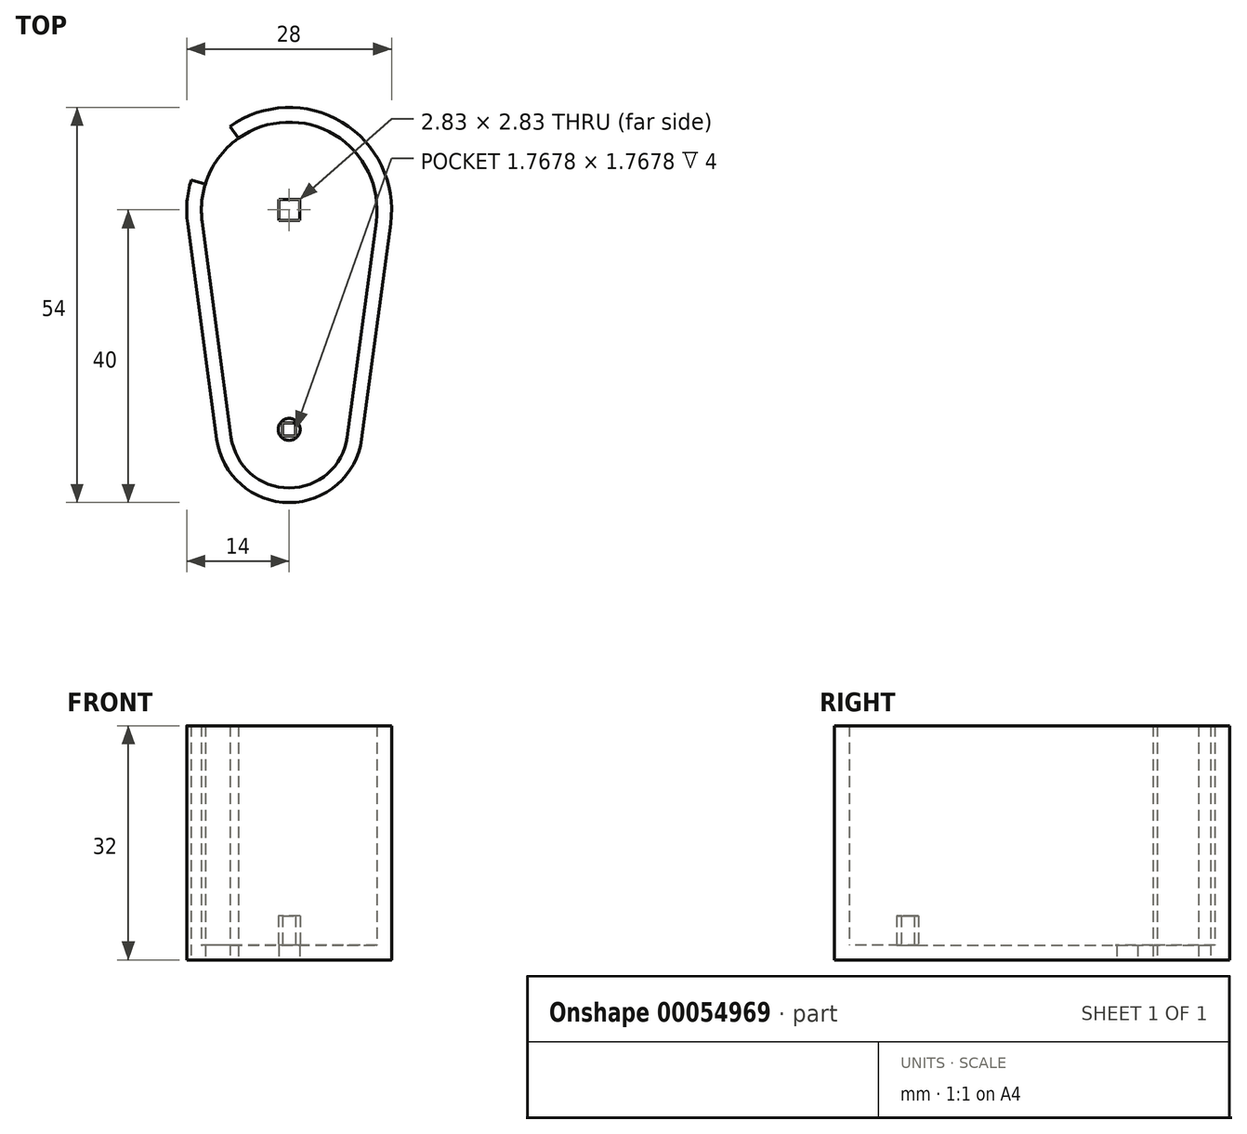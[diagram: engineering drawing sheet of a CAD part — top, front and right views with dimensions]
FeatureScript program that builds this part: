
annotation { "Feature Type Name" : "Feature", "Feature Type Description" : "" }
export const myFeature = defineFeature(function(context is Context, id is Id, definition is map)
    precondition{}
    {
        {
            var Q0;
            Q0=qCreatedBy(makeId("Top.planeOp"),FACE);
            var sketch = newSketch(context, id + "F0", { "sketchPlane" : qUnion([Q0])});
            skArc(sketch, "E0", {"start": v(13.87, -1.87) * mm, "mid": v(0, 14) * mm, "end": v(-13.87, -1.87) * mm});
            skArc(sketch, "E1", {"start": v(-9.91, -31.33) * mm, "mid": v(0, -40) * mm, "end": v(9.91, -31.33) * mm});
            skLineSegment(sketch, "E2", {"start": v(-13.87, -1.87) * mm, "end": v(-9.91, -31.33) * mm});
            skLineSegment(sketch, "E3", {"start": v(13.87, -1.87) * mm, "end": v(9.91, -31.33) * mm});
            skCircle(sketch, "E4", {"center": v(0, -30) * mm, "radius": 8 * mm});
            skCircle(sketch, "E5", {"center": v(0, 0) * mm, "radius": 12 * mm});
            skLineSegment(sketch, "E6", {"start": v(7.93, -31.07) * mm, "end": v(11.9, -1.6) * mm});
            skLineSegment(sketch, "E7", {"start": v(-7.93, -31.07) * mm, "end": v(-12.1, 0) * mm});
            skCircle(sketch, "E8", {"center": v(0, -30) * mm, "radius": 4.9 * mm});
            skCircle(sketch, "E9", {"center": v(0, -30) * mm, "radius": 2.95 * mm});
            skCircle(sketch, "E10", {"center": v(0, -30) * mm, "radius": 1.5 * mm});
            skCircle(sketch, "E11", {"center": v(0, 0) * mm, "radius": 4 * mm});
            skCircle(sketch, "E12", {"center": v(0, 0) * mm, "radius": 2.5 * mm});
            skLineSegment(sketch, "E13", {"start": v(-9.42, -20) * mm, "end": v(9.05, -20) * mm, "construction": true});
            skArc(sketch, "E14", {"start": v(-9.08, -22.48) * mm, "mid": v(-4.43, -19.6) * mm, "end": v(-9.68, -18.05) * mm});
            skArc(sketch, "E15", {"start": v(9.68, -18.05) * mm, "mid": v(4.43, -19.6) * mm, "end": v(9.08, -22.48) * mm});
            skArc(sketch, "E16", {"start": v(9.84, -16.83) * mm, "mid": v(3.44, -19.47) * mm, "end": v(8.92, -23.7) * mm});
            skArc(sketch, "E17", {"start": v(-8.92, -23.7) * mm, "mid": v(-3.44, -19.47) * mm, "end": v(-9.84, -16.83) * mm});
            skLineSegment(sketch, "E18", {"start": v(-8.1, 11.42) * mm, "end": v(-6.95, 9.78) * mm});
            skLineSegment(sketch, "E19", {"start": v(-13.39, 4.1) * mm, "end": v(-11.48, 3.5) * mm});
            skLineSegment(sketch, "E20.bottom", {"start": v(-1.41, 1.41) * mm, "end": v(1.41, 1.41) * mm});
            skLineSegment(sketch, "E20.top", {"start": v(-1.41, -1.41) * mm, "end": v(1.41, -1.41) * mm});
            skLineSegment(sketch, "E20.left", {"start": v(-1.41, 1.41) * mm, "end": v(-1.41, -1.41) * mm});
            skLineSegment(sketch, "E20.right", {"start": v(1.41, 1.41) * mm, "end": v(1.41, -1.41) * mm});
            skLineSegment(sketch, "E21.bottom", {"start": v(-0.88, -29.12) * mm, "end": v(0.88, -29.12) * mm});
            skLineSegment(sketch, "E21.top", {"start": v(-0.88, -30.88) * mm, "end": v(0.88, -30.88) * mm});
            skLineSegment(sketch, "E21.left", {"start": v(-0.88, -29.12) * mm, "end": v(-0.88, -30.88) * mm});
            skLineSegment(sketch, "E21.right", {"start": v(0.88, -29.12) * mm, "end": v(0.88, -30.88) * mm});
            skLineSegment(sketch, "E22", {"start": v(4, 0) * mm, "end": v(-4, 0) * mm, "construction": true});
            skLineSegment(sketch, "E23", {"start": v(0, 4) * mm, "end": v(0, -4) * mm, "construction": true});
            skLineSegment(sketch, "E24", {"start": v(-1.41, 1.41) * mm, "end": v(1.41, -1.41) * mm, "construction": true});
            skLineSegment(sketch, "E25", {"start": v(1.41, 1.41) * mm, "end": v(-1.41, -1.41) * mm, "construction": true});
            skLineSegment(sketch, "E26", {"start": v(-0.88, -30.88) * mm, "end": v(0.88, -29.12) * mm, "construction": true});
            skLineSegment(sketch, "E27", {"start": v(-0.88, -29.12) * mm, "end": v(0.88, -30.88) * mm, "construction": true});
            skLineSegment(sketch, "E28", {"start": v(0, -28.5) * mm, "end": v(0, -31.5) * mm, "construction": true});
            skLineSegment(sketch, "E29", {"start": v(-1.5, -30) * mm, "end": v(1.5, -30) * mm, "construction": true});
            skSolve(sketch);
        }
        {
            var Q0;
            Q0=makeQuery(id+"F0.imprint","IMPRINT",FACE,{"disambiguationData":[TD([[makeQuery(id+"F0.imprint","IMPRINT",EDGE,{"derivedFrom":sQuery(id+"F0.wireOp",EDGE,"E1")}),1.0]])]});
            extrude(context, id + "F1", {"entities" : qUnion([Q0]), "depth" : 32 * mm});
        }
        {
            var Q0;
            Q0=makeQuery(id+"F0.imprint","IMPRINT",FACE,{"disambiguationData":[TD([[makeQuery(id+"F0.imprint","IMPRINT",EDGE,{"derivedFrom":sQuery(id+"F0.wireOp",EDGE,"E11")}),-1.0]])]});
            var Q1;
            {var subQ3=sQuery(id+"F0.wireOp",EDGE,"E16");Q1=makeQuery(id+"F0.imprint","IMPRINT",FACE,{"disambiguationData":[TD([[makeQuery(id+"F0.imprint","IMPRINT",EDGE,{"derivedFrom":subQ3}),-1.0]])]});}
            var Q2;
            Q2=makeQuery(id+"F0.imprint","IMPRINT",FACE,{"disambiguationData":[TD([[makeQuery(id+"F0.imprint","IMPRINT",EDGE,{"derivedFrom":sQuery(id+"F0.wireOp",EDGE,"E8")}),-1.0]])]});
            var Q3;
            {var subQ0=sQuery(id+"F0.wireOp",EDGE,"E15");Q3=makeQuery(id+"F0.imprint","IMPRINT",FACE,{"disambiguationData":[TD([[makeQuery(id+"F0.imprint","IMPRINT",EDGE,{"derivedFrom":subQ0}),-1.0]])]});}
            var Q4;
            {var subQ0=sQuery(id+"F0.wireOp",EDGE,"E14");Q4=makeQuery(id+"F0.imprint","IMPRINT",FACE,{"disambiguationData":[TD([[makeQuery(id+"F0.imprint","IMPRINT",EDGE,{"derivedFrom":subQ0}),-1.0]])]});}
            var Q5;
            {var subQ0=sQuery(id+"F0.wireOp",EDGE,"E14");Q5=makeQuery(id+"F0.imprint","IMPRINT",FACE,{"disambiguationData":[TD([[makeQuery(id+"F0.imprint","IMPRINT",EDGE,{"derivedFrom":subQ0}),1.0]])]});}
            var Q6;
            Q6=makeQuery(id+"F0.imprint","IMPRINT",FACE,{"disambiguationData":[TD([[makeQuery(id+"F0.imprint","IMPRINT",EDGE,{"derivedFrom":sQuery(id+"F0.wireOp",EDGE,"E8")}),1.0]])]});
            var Q7;
            Q7=makeQuery(id+"F0.imprint","IMPRINT",FACE,{"disambiguationData":[TD([[makeQuery(id+"F0.imprint","IMPRINT",EDGE,{"derivedFrom":sQuery(id+"F0.wireOp",EDGE,"E9")}),1.0]])]});
            var Q8;
            Q8=makeQuery(id+"F0.imprint","IMPRINT",FACE,{"disambiguationData":[TD([[makeQuery(id+"F0.imprint","IMPRINT",EDGE,{"derivedFrom":sQuery(id+"F0.wireOp",EDGE,"E20.bottom")}),-1.0]])]});
            var Q9;
            Q9=makeQuery(id+"F0.imprint","IMPRINT",FACE,{"disambiguationData":[TD([[makeQuery(id+"F0.imprint","IMPRINT",EDGE,{"derivedFrom":sQuery(id+"F0.wireOp",EDGE,"E12")}),1.0]])]});
            var Q10;
            Q10=makeQuery(id+"F0.imprint","IMPRINT",FACE,{"disambiguationData":[TD([[makeQuery(id+"F0.imprint","IMPRINT",EDGE,{"derivedFrom":sQuery(id+"F0.wireOp",EDGE,"E11")}),1.0]])]});
            var Q11;
            Q11=makeQuery(id+"F0.imprint","IMPRINT",FACE,{"disambiguationData":[TD([[makeQuery(id+"F0.imprint","IMPRINT",EDGE,{"derivedFrom":sQuery(id+"F0.wireOp",EDGE,"E21.bottom")}),-1.0]])]});
            var Q12;
            Q12=makeQuery(id+"F0.imprint","IMPRINT",FACE,{"disambiguationData":[TD([[makeQuery(id+"F0.imprint","IMPRINT",EDGE,{"derivedFrom":sQuery(id+"F0.wireOp",EDGE,"E10")}),1.0]])]});
            var Q13;
            {var subQ0=sQuery(id+"F0.wireOp",EDGE,"E15");Q13=makeQuery(id+"F0.imprint","IMPRINT",FACE,{"disambiguationData":[TD([[makeQuery(id+"F0.imprint","IMPRINT",EDGE,{"derivedFrom":subQ0}),1.0]])]});}
            extrude(context, id + "F2", {"entities" : qUnion([Q0, Q1, Q2, Q3, Q4, Q5, Q6, Q7, Q8, Q9, Q10, Q11, Q12, Q13]), "operationType" : NewBodyOperationType.ADD, "depth" : 2 * mm});
        }
        {
            var Q0;
            Q0=makeQuery(id+"F0.imprint","IMPRINT",FACE,{"disambiguationData":[TD([[makeQuery(id+"F0.imprint","IMPRINT",EDGE,{"derivedFrom":sQuery(id+"F0.wireOp",EDGE,"E20.bottom")}),-1.0]])]});
            extrude(context, id + "F3", {"entities" : qUnion([Q0]), "operationType" : NewBodyOperationType.REMOVE, "depth" : 3 * mm});
        }
        {
            var Q0;
            Q0=makeQuery(id+"F0.imprint","IMPRINT",FACE,{"disambiguationData":[TD([[makeQuery(id+"F0.imprint","IMPRINT",EDGE,{"derivedFrom":sQuery(id+"F0.wireOp",EDGE,"E10")}),1.0]])]});
            extrude(context, id + "F4", {"entities" : qUnion([Q0]), "operationType" : NewBodyOperationType.ADD, "depth" : 6 * mm});
        }
    });
